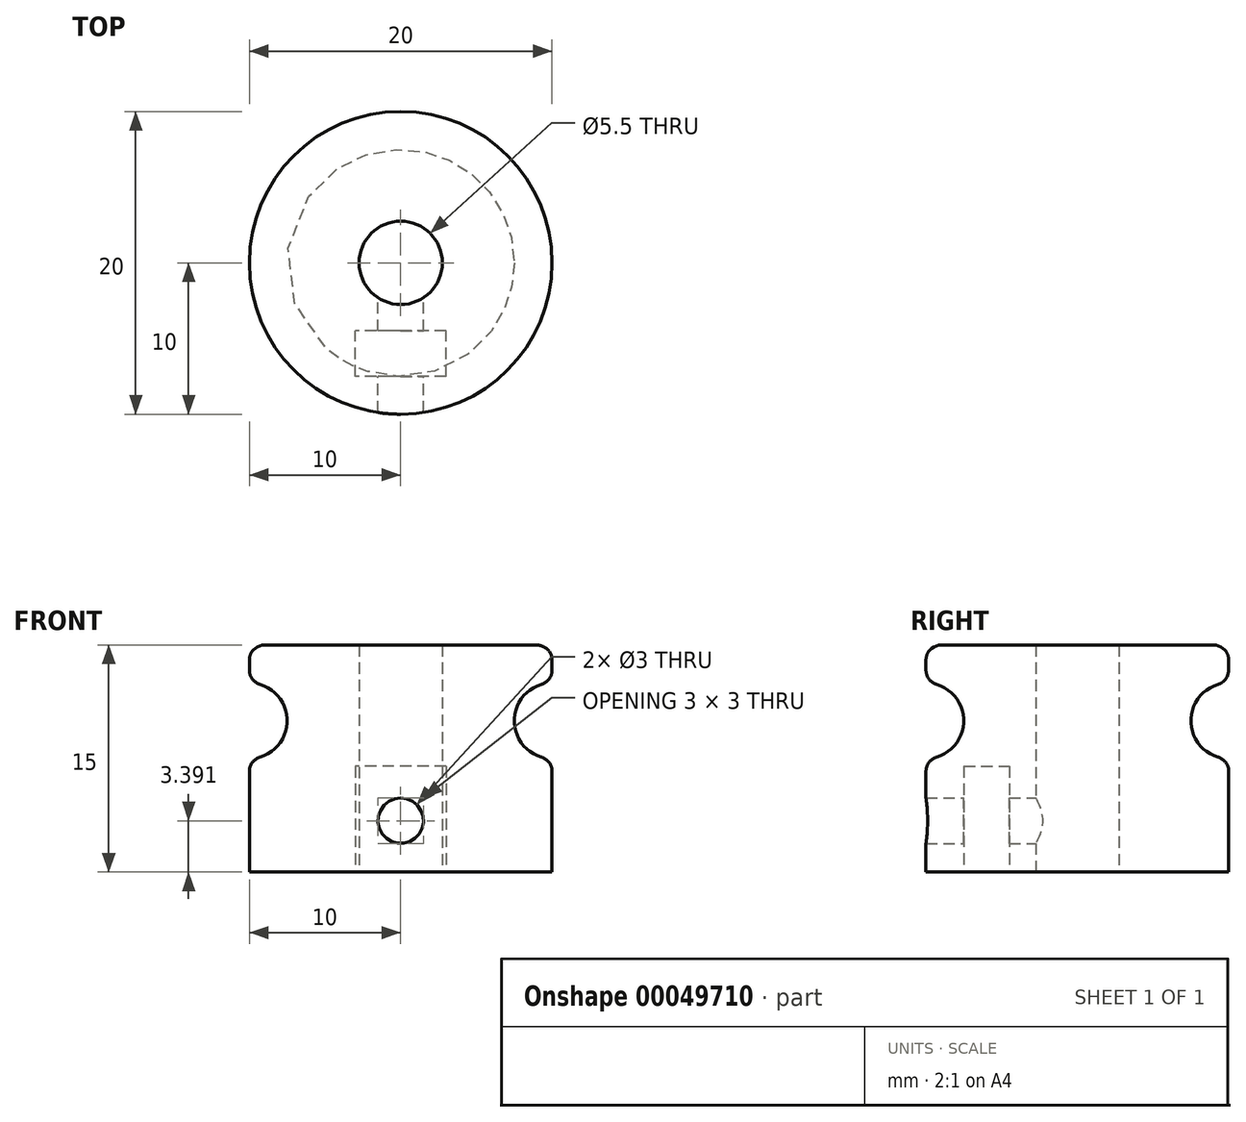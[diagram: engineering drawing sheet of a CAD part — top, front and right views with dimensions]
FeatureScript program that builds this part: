
annotation { "Feature Type Name" : "Feature", "Feature Type Description" : "" }
export const myFeature = defineFeature(function(context is Context, id is Id, definition is map)
    precondition{}
    {
        {
            var Q0;
            Q0=qCreatedBy(makeId("Top.planeOp"),FACE);
            var sketch = newSketch(context, id + "F0", { "sketchPlane" : qUnion([Q0])});
            skCircle(sketch, "E0", {"center": v(0, 0) * mm, "radius": 2.75 * mm});
            skCircle(sketch, "E1", {"center": v(0, 0) * mm, "radius": 10 * mm});
            skSolve(sketch);
        }
        {
            var Q0;
            Q0=makeQuery(id+"F0.imprint","IMPRINT",FACE,{"disambiguationData":[TD([[makeQuery(id+"F0.imprint","IMPRINT",EDGE,{"derivedFrom":sQuery(id+"F0.wireOp",EDGE,"E0")}),-1.0]])]});
            extrude(context, id + "F1", {"entities" : qUnion([Q0]), "depth" : 15 * mm});
        }
        {
            var Q0;
            Q0=qCreatedBy(makeId("Right.planeOp"),FACE);
            var sketch = newSketch(context, id + "F2", { "sketchPlane" : qUnion([Q0])});
            skCircle(sketch, "E2", {"center": v(-10, 10) * mm, "radius": 2.5 * mm});
            skSolve(sketch);
        }
        {
            var Q0;
            Q0=makeQuery(id+"F2.imprint","IMPRINT",FACE,{"disambiguationData":[TD([[makeQuery(id+"F2.imprint","IMPRINT",EDGE,{"derivedFrom":sQuery(id+"F2.wireOp",EDGE,"E2")}),1.0]])]});
            var Q1;
            Q1=makeQuery(id+"F1.opExtrude","CAP_EDGE",EDGE,{"disambiguationData":[OSD([sQuery(id+"F0.wireOp",EDGE,"E0")])],"isStart":false});
            revolve(context, id + "F3", {"operationType" : NewBodyOperationType.REMOVE, "entities" : qUnion([Q0]), "axis" : qUnion([Q1]), "revolveType" : RevolveType.FULL, "oppositeDirection" : true});
        }
        {
            var Q0;
            Q0=makeQuery(id+"F3.boolean.opBoolean","INTERSECT",EDGE,{"disambiguationData":[OD(0.0)],"derivedFrom":[makeQuery(id+"F1.opExtrude","SWEPT_FACE",FACE,{"disambiguationData":[OSD([sQuery(id+"F0.wireOp",EDGE,"E1")])]}),makeQuery(id+"F3.opRevolve","SWEPT_FACE",FACE,{"disambiguationData":[OSD([sQuery(id+"F2.wireOp",EDGE,"E2")])]})]});
            var Q1;
            Q1=makeQuery(id+"F3.boolean.opBoolean","INTERSECT",EDGE,{"disambiguationData":[OD(1.0)],"derivedFrom":[makeQuery(id+"F1.opExtrude","SWEPT_FACE",FACE,{"disambiguationData":[OSD([sQuery(id+"F0.wireOp",EDGE,"E1")])]}),makeQuery(id+"F3.opRevolve","SWEPT_FACE",FACE,{"disambiguationData":[OSD([sQuery(id+"F2.wireOp",EDGE,"E2")])]})]});
            var Q2;
            Q2=makeQuery(id+"F1.opExtrude","CAP_EDGE",EDGE,{"disambiguationData":[OSD([sQuery(id+"F0.wireOp",EDGE,"E1")])],"isStart":false});
            fillet(context, id + "F4", {"entities" : qUnion([Q0, Q1, Q2]), "radius" : 1 * mm, "tangentPropagation" : true, "allowEdgeOverflow" : false});
        }
        {
            var Q0;
            Q0=qCreatedBy(makeId("Front.planeOp"),FACE);
            var sketch = newSketch(context, id + "F5", { "sketchPlane" : qUnion([Q0])});
            skCircle(sketch, "E3", {"center": v(0, 3.4) * mm, "radius": 1.5 * mm});
            skSolve(sketch);
        }
        {
            var Q0;
            Q0 = qSketchRegion(id + "F5", true);
            extrude(context, id + "F6", {"entities" : qUnion([Q0]), "operationType" : NewBodyOperationType.REMOVE, "depth" : 25 * mm});
        }
        {
            var Q0;
            Q0=makeQuery(id+"F1.opExtrude","CAP_FACE",FACE,{"disambiguationData":[OSD([sQuery(id+"F0.wireOp",EDGE,"E0"),sQuery(id+"F0.wireOp",EDGE,"E1")])],"isStart":true});
            var sketch = newSketch(context, id + "F7", { "sketchPlane" : qUnion([Q0])});
            skLineSegment(sketch, "E4.rect.bottom", {"start": v(3, 7.5) * mm, "end": v(-3, 7.5) * mm});
            skLineSegment(sketch, "E4.rect.top", {"start": v(3, 4.5) * mm, "end": v(-3, 4.5) * mm});
            skLineSegment(sketch, "E4.rect.left", {"start": v(3, 7.5) * mm, "end": v(3, 4.5) * mm});
            skLineSegment(sketch, "E4.rect.right", {"start": v(-3, 7.5) * mm, "end": v(-3, 4.5) * mm});
            skPoint(sketch, "E4.rect.middle", {"position": v(0, 6) * mm});
            skSolve(sketch);
        }
        {
            var Q0;
            Q0=makeQuery(id+"F7.imprint","IMPRINT",FACE,{"disambiguationData":[TD([[makeQuery(id+"F7.imprint","IMPRINT",EDGE,{"derivedFrom":sQuery(id+"F7.wireOp",EDGE,"E4.rect.bottom")}),1.0]])]});
            extrude(context, id + "F8", {"entities" : qUnion([Q0]), "operationType" : NewBodyOperationType.REMOVE, "oppositeDirection" : true, "depth" : 7 * mm});
        }
    });
